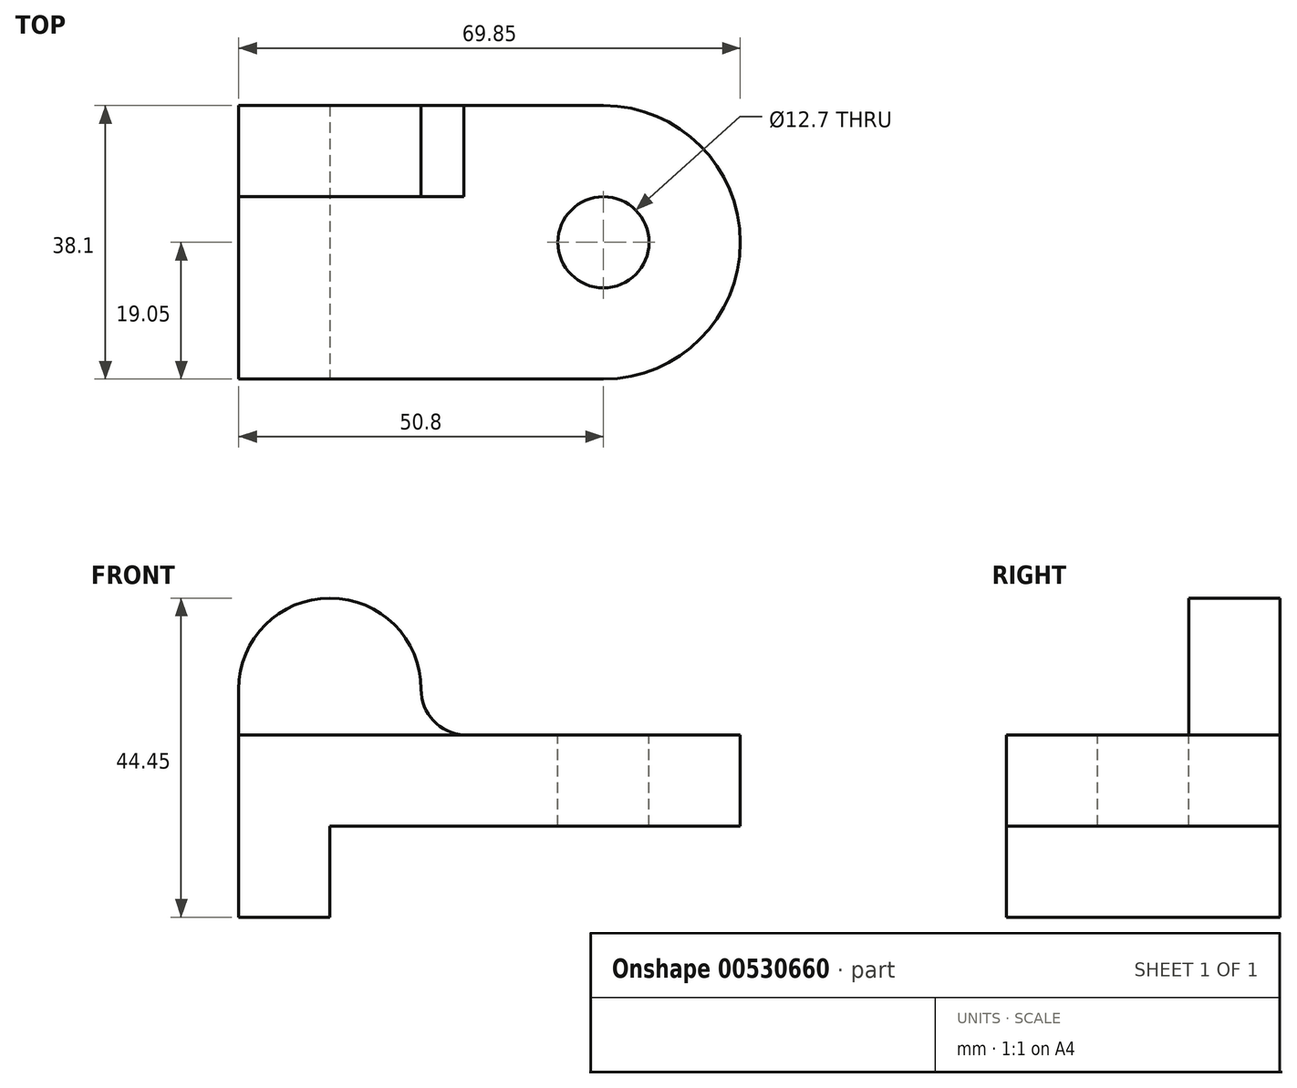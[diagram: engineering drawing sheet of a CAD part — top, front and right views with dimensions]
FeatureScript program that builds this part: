
annotation { "Feature Type Name" : "Feature", "Feature Type Description" : "" }
export const myFeature = defineFeature(function(context is Context, id is Id, definition is map)
    precondition{}
    {
        {
            var Q0;
            Q0=qCreatedBy(makeId("Top.planeOp"),FACE);
            var sketch = newSketch(context, id + "F0", { "sketchPlane" : qUnion([Q0])});
            skLineSegment(sketch, "E0", {"start": v(0, 0) * mm, "end": v(0, 38.1) * mm});
            skLineSegment(sketch, "E1", {"start": v(0, 38.1) * mm, "end": v(50.8, 38.1) * mm});
            skLineSegment(sketch, "E2", {"start": v(50.8, 0) * mm, "end": v(0, 0) * mm});
            skArc(sketch, "E3", {"start": v(50.8, 0) * mm, "mid": v(69.85, 19.05) * mm, "end": v(50.8, 38.1) * mm});
            skLineSegment(sketch, "E4", {"start": v(12.7, 38.1) * mm, "end": v(12.7, 0) * mm});
            skCircle(sketch, "E5", {"center": v(50.8, 19.05) * mm, "radius": 6.35 * mm});
            skSolve(sketch);
        }
        {
            var Q0;
            {var subQ1=sQuery(id+"F0.wireOp",EDGE,"E3");Q0=makeQuery(id+"F0.imprint","IMPRINT",FACE,{"disambiguationData":[TD([[makeQuery(id+"F0.imprint","IMPRINT",EDGE,{"derivedFrom":subQ1}),1.0]])]});}
            extrude(context, id + "F1", {"entities" : qUnion([Q0]), "oppositeDirection" : true, "depth" : 12.7 * mm, "offsetDistance" : 25.4 * mm});
        }
        {
            var Q0;
            {var subQ0=sQuery(id+"F0.wireOp",EDGE,"E0");Q0=makeQuery(id+"F0.imprint","IMPRINT",FACE,{"disambiguationData":[TD([[makeQuery(id+"F0.imprint","IMPRINT",EDGE,{"derivedFrom":subQ0}),-1.0]])]});}
            extrude(context, id + "F2", {"entities" : qUnion([Q0]), "operationType" : NewBodyOperationType.ADD, "oppositeDirection" : true, "depth" : 25.4 * mm, "offsetDistance" : 25.4 * mm});
        }
        {
            var Q0;
            {var subQ0=sQuery(id+"F0.wireOp",EDGE,"E1");Q0=makeQuery(id+"F2.boolean.opBoolean","MERGE",FACE,{"derivedFrom":[makeQuery(id+"F1.opExtrude","SWEPT_FACE",FACE,{"disambiguationData":[OSD([subQ0])]}),makeQuery(id+"F2.opExtrude","SWEPT_FACE",FACE,{"disambiguationData":[OSD([subQ0])]})]});}
            var sketch = newSketch(context, id + "F3", { "sketchPlane" : qUnion([Q0])});
            skLineSegment(sketch, "E6", {"start": v(0, 0) * mm, "end": v(0, 6.35) * mm});
            skLineSegment(sketch, "E7", {"start": v(0, 0) * mm, "end": v(-25.4, 0) * mm});
            skArc(sketch, "E8", {"start": v(0, 6.35) * mm, "mid": v(-12.7, 19.05) * mm, "end": v(-25.4, 6.35) * mm});
            skArc(sketch, "E9", {"start": v(-31.38, 0) * mm, "mid": v(-27.13, 1.99) * mm, "end": v(-25.4, 6.35) * mm});
            skSolve(sketch);
        }
        {
            var Q0;
            Q0=makeQuery(id+"F3.imprint","IMPRINT",FACE,{"disambiguationData":[TD([[makeQuery(id+"F3.imprint","IMPRINT",EDGE,{"derivedFrom":sQuery(id+"F3.wireOp",EDGE,"E6")}),1.0]])]});
            extrude(context, id + "F4", {"entities" : qUnion([Q0]), "operationType" : NewBodyOperationType.ADD, "oppositeDirection" : true, "depth" : 12.7 * mm, "offsetDistance" : 25.4 * mm});
        }
    });
